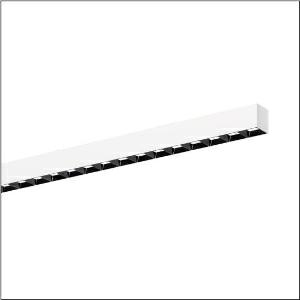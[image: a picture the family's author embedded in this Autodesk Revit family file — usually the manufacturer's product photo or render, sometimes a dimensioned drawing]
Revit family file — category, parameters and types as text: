
# Revit family: silica_r__21_51mx24tctaw_1b94
name_source: partatom
category: Lighting Fixtures
units: mm (PartAtom-declared; Revit-internal decimal feet)

## family parameters
Cut with Voids When Loaded = No
Host = Face
Light Source = No
Part Type = Normal
Room Calculation Point = No
Round Connector Dimension = Use Diameter
Shared = No

## types (1)
- --- (1 x LED, 8200 lm, 81.1 W, 6500K)
    Apparent Load = 81 VA
    CIE Flux Codes = 74 94 99 100 100
    Color Rendering = 80
    Color Temperature = 6500K
    Default Elevation = 1800 mm
    Description = Silica® 21, office luminaire, primary light control with darklight reflector, of PMMA, black, light emission: direct distribution, primary light characteristic: asymmetric, installation type: surface-mounted, LED, rated luminous flux: 8.200lm, luminous efficacy: 96lm/W, light colour: 8tw, colour temperature: 2700..6500K, control gear: ECG DALI, with terminal, 3+2-pole, max. 2.5mm², mains connection: 220..240V, AC, 50/60Hz, rated input power: 85.2W, luminaire housing, of aluminium, traffic white (RAL 9016), length: 3.004mm, width: 53mm, height: 53mm, protection rating (complete): IP20, insulation class (complete): insulation class I (protective earthing), certification: CE, permissible operating ambient temperature: 0..+35°C, standard: EN 50419, packaging unit: 1 piece
    Height = 0 mm  [stored 0 ft]
    Lamp = 1 x LED
    Lamp Light Flux = 8200 lm
    Lamp Power = 81.1 W
    Lamp count = 1
    Length = 3004 mm
    Luminous efficacy = 101 lm/W
    Manufacturer = Siteco
    ModVariant = No
    Model = 51MX24TCTAW
    Mounting Place = Ceiling
    Mounting Type = Recessed
    Number of Poles = 1
    OnlyDefault = Yes
    Power Factor = 1
    Product Name = Silica® 21
    Product group = office luminaire | ceiling recessed
    ProductGroupID = 401
    Protection Class = Protection class I
    Protection Degree = IP 20
    RLX_Detail_Level = 1
    RLX_Emergency_Light_Flux = 0 lm
    RLX_Emergency_Type = 0
    RLX_Emergency_Type_DB = No
    RlxData = <blob elided: 59237 chars, md5=de771f07>
    Socket = socket
    Standby Power = 0 W
    System Light Flux = 8200 lm
    System Power = 81 W
    Type Comments = individual setting
    Type Image = l_1297779.jpg
    URL = http://relux.com
    VarID = @adj_071329
    Voltage = 0 V
    Weight = 0.00 kg
    Width = 53 mm

note: [stored X ft] marks values corroborated as IEEE doubles in the binary element streams (Revit-internal decimal feet)

## geometry (parser evidence)
native form markers: Blend x4, Sweep x10
no freeform markers — native parametric forms only
